# Revit family: Bathtub_Transitional_Nexus_FBF794S_TOTO
name_source: partatom
category: Plumbing Fixtures
revit_build: Autodesk Revit Architecture 2013 (Build: 20130531_2115(x64)
units: mm (PartAtom-declared; Revit-internal decimal feet)

## types (1)
- FBF794S#01D
    04 CSI = 22 41 19
    95 CSI = 15410
    Assembly Code = D2010510
    Bottom Plate = Metal - TOTO - LifeKoat - Brass - Polished
    CAD Drawing URL = http://assets.totousa.com
    CW Connection = No
    CWFU = 0
    Color Availability = #01  Cotton
    Default Elevation = 0"
    Depth = 66 15/16"
    Description = Cast Iron Bathtub
    Finish = Metal - TOTO - Chrome - Polished
    HW Connection = No
    HWFU = 0
    Height = 21 1/8"
    Manufacturer = TOTO USA, Inc.
    Manufacturer Fax = (770) 282-0002
    Model = FBF794S#01D
    Series = Nexus
    Shipping Weight = 390.00 lb
    Spec Sheet URL = http://assets.totousa.com
    Style = Transitional
    Subcategory = Bathtubs
    Toto BIM Number = BM-00157
    URL = http://www.totousa.com
    Vent Connection = Yes
    WFU = 0
    Warranty = Lifetime Limited Warranty
    Warranty URL = http://www.totousa.com
    Waste Connection = Yes
    Waste Connection NPT = 3"
    Waste Connection Radius = 1 1/2"
    Width = 29 17/32"

## geometry (parser evidence)
native form markers: Blend x24, Sweep x2
no freeform markers — native parametric forms only
